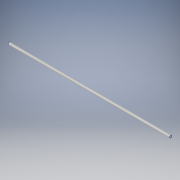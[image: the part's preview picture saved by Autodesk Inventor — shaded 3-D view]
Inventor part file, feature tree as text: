
AUTODESK INVENTOR PART (.ipt)
format: ipt  version: 2019 (Build 230136000, 136)  size: 95,232 bytes
history: native  units: mm
features: other x1, extrude x1, sketch x1
ambient origin geometry x8: Origin, YZ Plane, XZ Plane, XY Plane, X Axis, Y Axis, Z Axis, Center Point
bodies: Body1 (feature_tree)
feature tree (3):
  other  "ソリッド1"
  extrude  "押し出し1"  Depth=5.0mm
  sketch  "スケッチ1"
